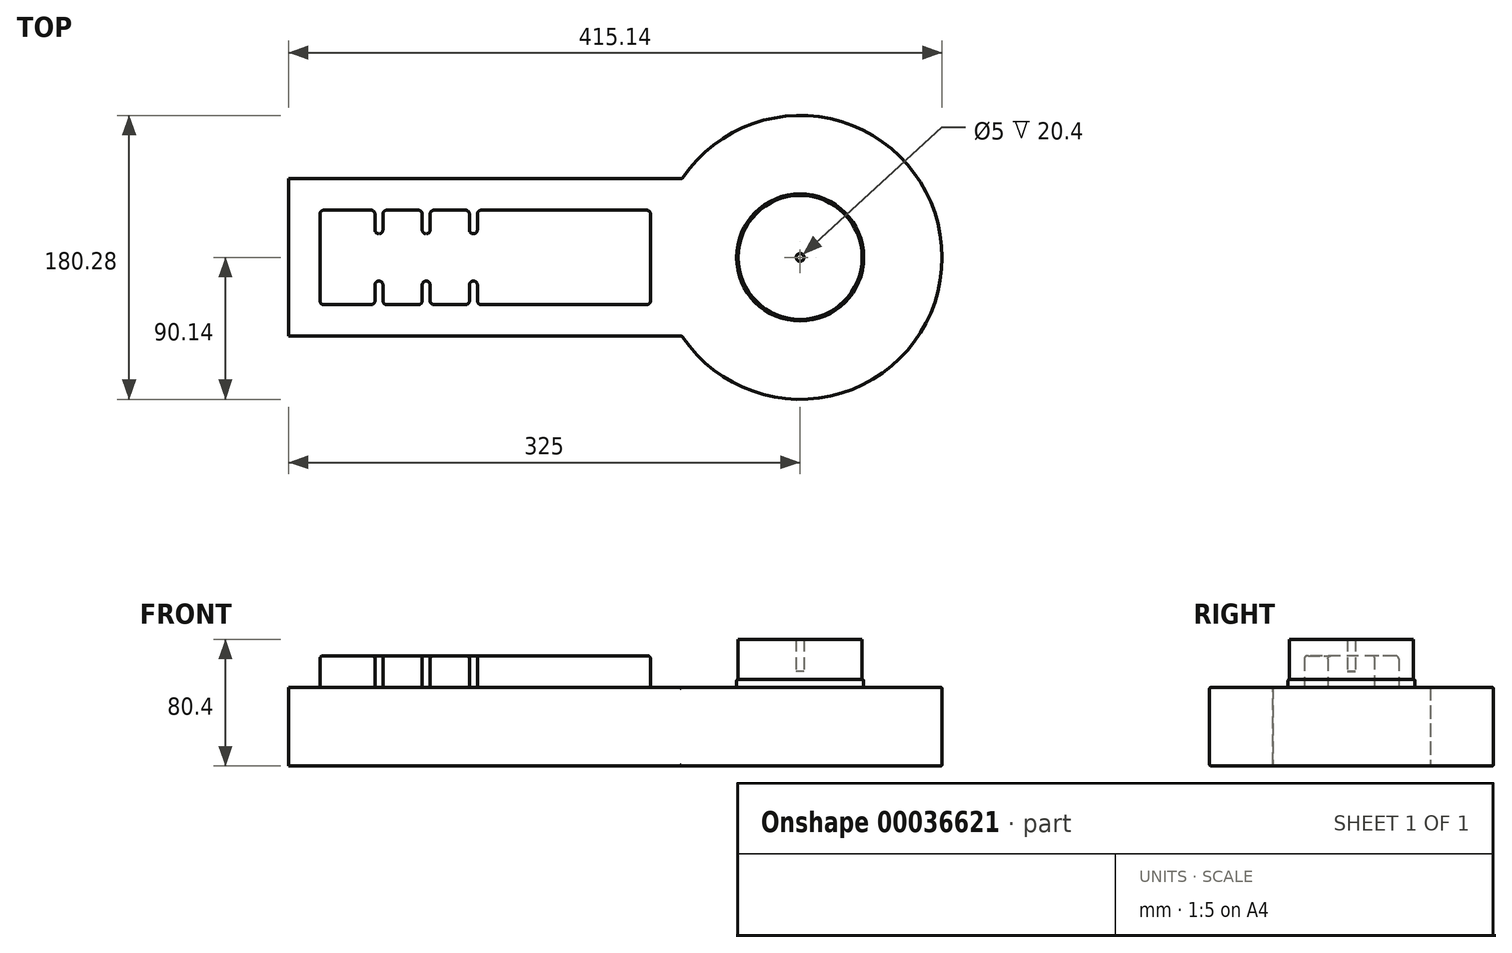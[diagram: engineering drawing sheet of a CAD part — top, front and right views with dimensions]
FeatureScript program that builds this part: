
annotation { "Feature Type Name" : "Feature", "Feature Type Description" : "" }
export const myFeature = defineFeature(function(context is Context, id is Id, definition is map)
    precondition{}
    {
        {
            var Q0;
            Q0=qCreatedBy(makeId("Top.planeOp"),FACE);
            var sketch = newSketch(context, id + "F0", { "sketchPlane" : qUnion([Q0])});
            skLineSegment(sketch, "E0.bottom", {"start": v(0, 0) * mm, "end": v(250, 0) * mm});
            skLineSegment(sketch, "E0.top", {"start": v(0, 100) * mm, "end": v(250, 100) * mm});
            skLineSegment(sketch, "E0.left", {"start": v(0, 0) * mm, "end": v(0, 100) * mm});
            skLineSegment(sketch, "E0.right", {"start": v(250, 0) * mm, "end": v(250, 100) * mm});
            skArc(sketch, "E1", {"start": v(250, 0) * mm, "mid": v(415.14, 50) * mm, "end": v(250, 100) * mm});
            skSolve(sketch);
        }
        {
            var Q0;
            Q0=makeQuery(id+"F0.imprint","IMPRINT",FACE,{"disambiguationData":[TD([[makeQuery(id+"F0.imprint","IMPRINT",EDGE,{"derivedFrom":sQuery(id+"F0.wireOp",EDGE,"E0.bottom")}),1.0]])]});
            var Q1;
            Q1=makeQuery(id+"F0.imprint","IMPRINT",FACE,{"disambiguationData":[TD([[makeQuery(id+"F0.imprint","IMPRINT",EDGE,{"derivedFrom":sQuery(id+"F0.wireOp",EDGE,"E0.right")}),-1.0]])]});
            extrude(context, id + "F1", {"entities" : qUnion([Q0, Q1]), "depth" : 50 * mm});
        }
        {
            var Q0;
            Q0=makeQuery(id+"F1.opExtrude","CAP_FACE",FACE,{"disambiguationData":[OSD([sQuery(id+"F0.wireOp",EDGE,"E0.bottom"),sQuery(id+"F0.wireOp",EDGE,"E0.top"),sQuery(id+"F0.wireOp",EDGE,"E0.left"),sQuery(id+"F0.wireOp",EDGE,"E1")])],"isStart":false});
            var sketch = newSketch(context, id + "F2", { "sketchPlane" : qUnion([Q0])});
            skLineSegment(sketch, "E2.bottom", {"start": v(20, 80) * mm, "end": v(230, 80) * mm});
            skLineSegment(sketch, "E2.top", {"start": v(20, 20) * mm, "end": v(230, 20) * mm});
            skLineSegment(sketch, "E2.left", {"start": v(20, 80) * mm, "end": v(20, 20) * mm});
            skLineSegment(sketch, "E2.right", {"start": v(230, 80) * mm, "end": v(230, 20) * mm});
            skLineSegment(sketch, "E3.bottom", {"start": v(55, 80) * mm, "end": v(60, 80) * mm});
            skLineSegment(sketch, "E3.top", {"start": v(55, 65) * mm, "end": v(60, 65) * mm});
            skLineSegment(sketch, "E3.left", {"start": v(55, 80) * mm, "end": v(55, 65) * mm});
            skLineSegment(sketch, "E3.right", {"start": v(60, 80) * mm, "end": v(60, 65) * mm});
            skLineSegment(sketch, "E4.bottom", {"start": v(85, 80) * mm, "end": v(90, 80) * mm});
            skLineSegment(sketch, "E4.top", {"start": v(85, 65) * mm, "end": v(90, 65) * mm});
            skLineSegment(sketch, "E4.left", {"start": v(85, 80) * mm, "end": v(85, 65) * mm});
            skLineSegment(sketch, "E4.right", {"start": v(90, 80) * mm, "end": v(90, 65) * mm});
            skLineSegment(sketch, "E5.bottom", {"start": v(115, 80) * mm, "end": v(120, 80) * mm});
            skLineSegment(sketch, "E5.top", {"start": v(115, 65) * mm, "end": v(120, 65) * mm});
            skLineSegment(sketch, "E5.left", {"start": v(115, 80) * mm, "end": v(115, 65) * mm});
            skLineSegment(sketch, "E5.right", {"start": v(120, 80) * mm, "end": v(120, 65) * mm});
            skLineSegment(sketch, "E6.bottom", {"start": v(55, 20) * mm, "end": v(60, 20) * mm});
            skLineSegment(sketch, "E6.top", {"start": v(55, 35) * mm, "end": v(60, 35) * mm});
            skLineSegment(sketch, "E6.left", {"start": v(55, 20) * mm, "end": v(55, 35) * mm});
            skLineSegment(sketch, "E6.right", {"start": v(60, 20) * mm, "end": v(60, 35) * mm});
            skLineSegment(sketch, "E7.bottom", {"start": v(85, 20) * mm, "end": v(90, 20) * mm});
            skLineSegment(sketch, "E7.top", {"start": v(85, 35) * mm, "end": v(90, 35) * mm});
            skLineSegment(sketch, "E7.left", {"start": v(85, 20) * mm, "end": v(85, 35) * mm});
            skLineSegment(sketch, "E7.right", {"start": v(90, 20) * mm, "end": v(90, 35) * mm});
            skLineSegment(sketch, "E8.bottom", {"start": v(115, 20) * mm, "end": v(120, 20) * mm});
            skLineSegment(sketch, "E8.top", {"start": v(115, 35) * mm, "end": v(120, 35) * mm});
            skLineSegment(sketch, "E8.left", {"start": v(115, 20) * mm, "end": v(115, 35) * mm});
            skLineSegment(sketch, "E8.right", {"start": v(120, 20) * mm, "end": v(120, 35) * mm});
            skSolve(sketch);
        }
        {
            var Q0;
            {var subQ20=sQuery(id+"F2.wireOp",EDGE,"E2.left");Q0=makeQuery(id+"F2.imprint","IMPRINT",FACE,{"disambiguationData":[TD([[makeQuery(id+"F2.imprint","IMPRINT",EDGE,{"derivedFrom":subQ20}),1.0]])]});}
            extrude(context, id + "F3", {"entities" : qUnion([Q0]), "operationType" : NewBodyOperationType.ADD, "depth" : 20 * mm});
        }
        {
            var Q0;
            Q0=makeQuery(id+"F1.opExtrude","CAP_FACE",FACE,{"disambiguationData":[OSD([sQuery(id+"F0.wireOp",EDGE,"E0.bottom"),sQuery(id+"F0.wireOp",EDGE,"E0.top"),sQuery(id+"F0.wireOp",EDGE,"E0.left"),sQuery(id+"F0.wireOp",EDGE,"E1")])],"isStart":false});
            var sketch = newSketch(context, id + "F4", { "sketchPlane" : qUnion([Q0])});
            skCircle(sketch, "E9", {"center": v(325, 50) * mm, "radius": 40.38 * mm});
            skSolve(sketch);
        }
        {
            var Q0;
            Q0=qSketchRegion(id+"F4",true);
            extrude(context, id + "F5", {"entities" : qUnion([Q0]), "operationType" : NewBodyOperationType.ADD, "depth" : 5 * mm});
        }
        {
            var Q0;
            Q0=makeQuery(id+"F5.opExtrude","CAP_FACE",FACE,{"disambiguationData":[OSD([sQuery(id+"F4.wireOp",EDGE,"E9")])],"isStart":false});
            var sketch = newSketch(context, id + "F6", { "sketchPlane" : qUnion([Q0])});
            skCircle(sketch, "E10", {"center": v(325, 50) * mm, "radius": 2.5 * mm});
            skSolve(sketch);
        }
        {
            var Q0;
            Q0=makeQuery(id+"F6.imprint","IMPRINT",FACE,{"disambiguationData":[TD([[makeQuery(id+"F6.imprint","IMPRINT",EDGE,{"derivedFrom":sQuery(id+"F6.wireOp",EDGE,"E10")}),1.0]])]});
            extrude(context, id + "F7", {"entities" : qUnion([Q0]), "operationType" : NewBodyOperationType.ADD, "depth" : 5 * mm});
        }
        {
            var Q0;
            Q0=makeQuery(id+"F1.opExtrude","SWEPT_FACE",FACE,{"disambiguationData":[OSD([sQuery(id+"F0.wireOp",EDGE,"E1")])]});
            var Q1;
            Q1=makeQuery(id+"F5.opExtrude","CAP_EDGE",EDGE,{"disambiguationData":[OSD([sQuery(id+"F4.wireOp",EDGE,"E9")])],"isStart":false});
            var Q2;
            Q2=makeQuery(id+"F5.opExtrude","CAP_EDGE",EDGE,{"disambiguationData":[OSD([sQuery(id+"F4.wireOp",EDGE,"E9")])],"isStart":true});
            fillet(context, id + "F8", {"entities" : qUnion([Q0, Q1, Q2]), "radius" : 1 * mm, "tangentPropagation" : true, "allowEdgeOverflow" : false});
        }
        {
            var Q0;
            Q0=makeQuery(id+"F3.opExtrude","SWEPT_EDGE",EDGE,{"disambiguationData":[OSD([sQuery(id+"F2.wireOp",EDGE,"E6.top"),sQuery(id+"F2.wireOp",EDGE,"E6.left")])]});
            var Q1;
            Q1=makeQuery(id+"F3.opExtrude","SWEPT_EDGE",EDGE,{"disambiguationData":[OSD([sQuery(id+"F2.wireOp",EDGE,"E2.top"),sQuery(id+"F2.wireOp",EDGE,"E6.bottom"),sQuery(id+"F2.wireOp",EDGE,"E6.left")])]});
            var Q2;
            Q2=makeQuery(id+"F3.opExtrude","SWEPT_EDGE",EDGE,{"disambiguationData":[OSD([sQuery(id+"F2.wireOp",EDGE,"E6.top"),sQuery(id+"F2.wireOp",EDGE,"E6.right")])]});
            var Q3;
            Q3=makeQuery(id+"F3.opExtrude","SWEPT_EDGE",EDGE,{"disambiguationData":[OSD([sQuery(id+"F2.wireOp",EDGE,"E2.top"),sQuery(id+"F2.wireOp",EDGE,"E6.bottom"),sQuery(id+"F2.wireOp",EDGE,"E6.right")])]});
            var Q4;
            Q4=makeQuery(id+"F3.opExtrude","SWEPT_EDGE",EDGE,{"disambiguationData":[OSD([sQuery(id+"F2.wireOp",EDGE,"E2.top"),sQuery(id+"F2.wireOp",EDGE,"E7.bottom"),sQuery(id+"F2.wireOp",EDGE,"E7.left")])]});
            var Q5;
            Q5=makeQuery(id+"F3.opExtrude","SWEPT_EDGE",EDGE,{"disambiguationData":[OSD([sQuery(id+"F2.wireOp",EDGE,"E7.top"),sQuery(id+"F2.wireOp",EDGE,"E7.right")])]});
            var Q6;
            Q6=makeQuery(id+"F3.opExtrude","SWEPT_EDGE",EDGE,{"disambiguationData":[OSD([sQuery(id+"F2.wireOp",EDGE,"E2.top"),sQuery(id+"F2.wireOp",EDGE,"E7.bottom"),sQuery(id+"F2.wireOp",EDGE,"E7.right")])]});
            var Q7;
            Q7=makeQuery(id+"F3.opExtrude","SWEPT_EDGE",EDGE,{"disambiguationData":[OSD([sQuery(id+"F2.wireOp",EDGE,"E2.top"),sQuery(id+"F2.wireOp",EDGE,"E8.bottom"),sQuery(id+"F2.wireOp",EDGE,"E8.left")])]});
            var Q8;
            Q8=makeQuery(id+"F3.opExtrude","SWEPT_EDGE",EDGE,{"disambiguationData":[OSD([sQuery(id+"F2.wireOp",EDGE,"E8.top"),sQuery(id+"F2.wireOp",EDGE,"E8.right")])]});
            var Q9;
            Q9=makeQuery(id+"F3.opExtrude","SWEPT_EDGE",EDGE,{"disambiguationData":[OSD([sQuery(id+"F2.wireOp",EDGE,"E2.top"),sQuery(id+"F2.wireOp",EDGE,"E8.bottom"),sQuery(id+"F2.wireOp",EDGE,"E8.right")])]});
            var Q10;
            Q10=makeQuery(id+"F3.opExtrude","SWEPT_EDGE",EDGE,{"disambiguationData":[OSD([sQuery(id+"F2.wireOp",EDGE,"E7.top"),sQuery(id+"F2.wireOp",EDGE,"E7.left")])]});
            var Q11;
            Q11=makeQuery(id+"F3.opExtrude","SWEPT_EDGE",EDGE,{"disambiguationData":[OSD([sQuery(id+"F2.wireOp",EDGE,"E8.top"),sQuery(id+"F2.wireOp",EDGE,"E8.left")])]});
            var Q12;
            Q12=makeQuery(id+"F3.opExtrude","SWEPT_EDGE",EDGE,{"disambiguationData":[OSD([sQuery(id+"F2.wireOp",EDGE,"E3.top"),sQuery(id+"F2.wireOp",EDGE,"E3.left")])]});
            var Q13;
            Q13=makeQuery(id+"F3.opExtrude","SWEPT_EDGE",EDGE,{"disambiguationData":[OSD([sQuery(id+"F2.wireOp",EDGE,"E2.bottom"),sQuery(id+"F2.wireOp",EDGE,"E3.bottom"),sQuery(id+"F2.wireOp",EDGE,"E3.left")])]});
            var Q14;
            Q14=makeQuery(id+"F3.opExtrude","SWEPT_EDGE",EDGE,{"disambiguationData":[OSD([sQuery(id+"F2.wireOp",EDGE,"E4.top"),sQuery(id+"F2.wireOp",EDGE,"E4.left")])]});
            var Q15;
            Q15=makeQuery(id+"F3.opExtrude","SWEPT_EDGE",EDGE,{"disambiguationData":[OSD([sQuery(id+"F2.wireOp",EDGE,"E2.bottom"),sQuery(id+"F2.wireOp",EDGE,"E4.bottom"),sQuery(id+"F2.wireOp",EDGE,"E4.left")])]});
            var Q16;
            Q16=makeQuery(id+"F3.opExtrude","SWEPT_EDGE",EDGE,{"disambiguationData":[OSD([sQuery(id+"F2.wireOp",EDGE,"E5.top"),sQuery(id+"F2.wireOp",EDGE,"E5.left")])]});
            var Q17;
            Q17=makeQuery(id+"F3.opExtrude","SWEPT_EDGE",EDGE,{"disambiguationData":[OSD([sQuery(id+"F2.wireOp",EDGE,"E2.bottom"),sQuery(id+"F2.wireOp",EDGE,"E5.bottom"),sQuery(id+"F2.wireOp",EDGE,"E5.left")])]});
            var Q18;
            Q18=makeQuery(id+"F3.opExtrude","SWEPT_EDGE",EDGE,{"disambiguationData":[OSD([sQuery(id+"F2.wireOp",EDGE,"E3.top"),sQuery(id+"F2.wireOp",EDGE,"E3.right")])]});
            var Q19;
            Q19=makeQuery(id+"F3.opExtrude","SWEPT_EDGE",EDGE,{"disambiguationData":[OSD([sQuery(id+"F2.wireOp",EDGE,"E2.bottom"),sQuery(id+"F2.wireOp",EDGE,"E3.bottom"),sQuery(id+"F2.wireOp",EDGE,"E3.right")])]});
            var Q20;
            Q20=makeQuery(id+"F3.opExtrude","SWEPT_EDGE",EDGE,{"disambiguationData":[OSD([sQuery(id+"F2.wireOp",EDGE,"E4.top"),sQuery(id+"F2.wireOp",EDGE,"E4.right")])]});
            var Q21;
            Q21=makeQuery(id+"F3.opExtrude","SWEPT_EDGE",EDGE,{"disambiguationData":[OSD([sQuery(id+"F2.wireOp",EDGE,"E2.bottom"),sQuery(id+"F2.wireOp",EDGE,"E4.bottom"),sQuery(id+"F2.wireOp",EDGE,"E4.right")])]});
            var Q22;
            Q22=makeQuery(id+"F3.opExtrude","SWEPT_EDGE",EDGE,{"disambiguationData":[OSD([sQuery(id+"F2.wireOp",EDGE,"E5.top"),sQuery(id+"F2.wireOp",EDGE,"E5.right")])]});
            var Q23;
            Q23=makeQuery(id+"F3.opExtrude","SWEPT_EDGE",EDGE,{"disambiguationData":[OSD([sQuery(id+"F2.wireOp",EDGE,"E2.bottom"),sQuery(id+"F2.wireOp",EDGE,"E5.bottom"),sQuery(id+"F2.wireOp",EDGE,"E5.right")])]});
            var Q24;
            Q24=makeQuery(id+"F3.opExtrude","SWEPT_EDGE",EDGE,{"disambiguationData":[OSD([sQuery(id+"F2.wireOp",EDGE,"E2.bottom"),sQuery(id+"F2.wireOp",EDGE,"E2.left")])]});
            var Q25;
            Q25=makeQuery(id+"F3.opExtrude","SWEPT_EDGE",EDGE,{"disambiguationData":[OSD([sQuery(id+"F2.wireOp",EDGE,"E2.top"),sQuery(id+"F2.wireOp",EDGE,"E2.left")])]});
            var Q26;
            Q26=makeQuery(id+"F3.opExtrude","SWEPT_EDGE",EDGE,{"disambiguationData":[OSD([sQuery(id+"F2.wireOp",EDGE,"E2.bottom"),sQuery(id+"F2.wireOp",EDGE,"E2.right")])]});
            var Q27;
            Q27=makeQuery(id+"F3.opExtrude","SWEPT_EDGE",EDGE,{"disambiguationData":[OSD([sQuery(id+"F2.wireOp",EDGE,"E2.top"),sQuery(id+"F2.wireOp",EDGE,"E2.right")])]});
            fillet(context, id + "F9", {"entities" : qUnion([Q0, Q1, Q2, Q3, Q4, Q5, Q6, Q7, Q8, Q9, Q10, Q11, Q12, Q13, Q14, Q15, Q16, Q17, Q18, Q19, Q20, Q21, Q22, Q23, Q24, Q25, Q26, Q27]), "radius" : 2.5 * mm, "tangentPropagation" : true, "allowEdgeOverflow" : false});
        }
        {
            var Q0;
            {var subQ0=sQuery(id+"F2.wireOp",EDGE,"E2.bottom");Q0=makeQuery(id+"F3.opExtrude","CAP_EDGE",EDGE,{"disambiguationData":[OSD([subQ0]),TDD([makeQuery(id+"F2.imprint","IMPRINT",EDGE,{"disambiguationData":[TD([[makeQuery(id+"F2.imprint","INTERSECT",VERTEX,{"derivedFrom":[subQ0,sQuery(id+"F2.wireOp",EDGE,"E2.right")]}),1.0]])],"derivedFrom":subQ0})])],"isStart":false});}
            var Q1;
            Q1=makeQuery(id+"F3.opExtrude","CAP_EDGE",EDGE,{"disambiguationData":[OSD([sQuery(id+"F2.wireOp",EDGE,"E2.right")])],"isStart":false});
            fillet(context, id + "F10", {"entities" : qUnion([Q0, Q1]), "radius" : 2 * mm, "tangentPropagation" : true, "allowEdgeOverflow" : false});
        }
        {
            var Q0;
            Q0=makeQuery(id+"F5.opExtrude","CAP_FACE",FACE,{"disambiguationData":[OSD([sQuery(id+"F4.wireOp",EDGE,"E9")])],"isStart":false});
            extrude(context, id + "F11", {"entities" : qUnion([Q0]), "operationType" : NewBodyOperationType.ADD, "depth" : 25.4 * mm});
        }
    });
